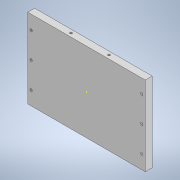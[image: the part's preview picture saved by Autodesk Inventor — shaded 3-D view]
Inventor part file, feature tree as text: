
AUTODESK INVENTOR PART (.ipt)
format: ipt  version: 2022.2 (Build 262287030, 287C)  size: 129,536 bytes
history: native  units: in
note: dims shown in document units (in); Inventor stores cm internally (conversion verified against a paired STEP export)
features: sketch x4, hole x3, extrude x1
ambient origin geometry x8: Origin, YZ Plane, XZ Plane, XY Plane, X Axis, Y Axis, Z Axis, Center Point
bodies: Solid1 (feature_tree)
feature tree (8):
  extrude  "Extrusion1"  Depth=4.5276in
  hole  "Hole1"  [1 undecoded]
  hole  "Hole2"  [1 undecoded]
  hole  "Hole3"  [1 undecoded]
  sketch  "Sketch5"  dims[d14=0.125in d15=0.2953in d16=0.1476in d17=0.0984in d18=90.0deg d19=0.1969in d20=0.0in d21=0.3937in d22=0.1969in d23=1.5748in d25=1.9685in d26=0.3937in d28=0.3937in d30=0.125in d31=0.2953in d32=0.1476in d33=0.0984in d34=90.0deg d35=0.1969in d36=0.0in d46=0.125in d47=0.2953in d48=0.1476in d49=0.0984in d50=90.0deg d51=0.1969in d52=0.0in d53=1.1811in d55=1.4764in d56=0.3937in d58=0.3937in d60=1.1811in d62=1.4764in d63=0.3937in d65=0.3937in d67=0.1969in d69=1.0827in d70=0.7874in d72=2.1654in d73=0.3937in d75=0.3937in]
  sketch  "Sketch1"  dims[d0=6.6929in d1=4.5276in]
  sketch  "Sketch3"  dims[d2=0.3937in d3=0.0in d4=0.1969in]
  sketch  "Sketch4"  dims[d5=0.7874in d11=6.2992in]
note: 3 required parameter values undecoded (feature->parameter linkage not recoverable at this tier; creation-order binding heuristic only, values carry confidence <= 0.55)
